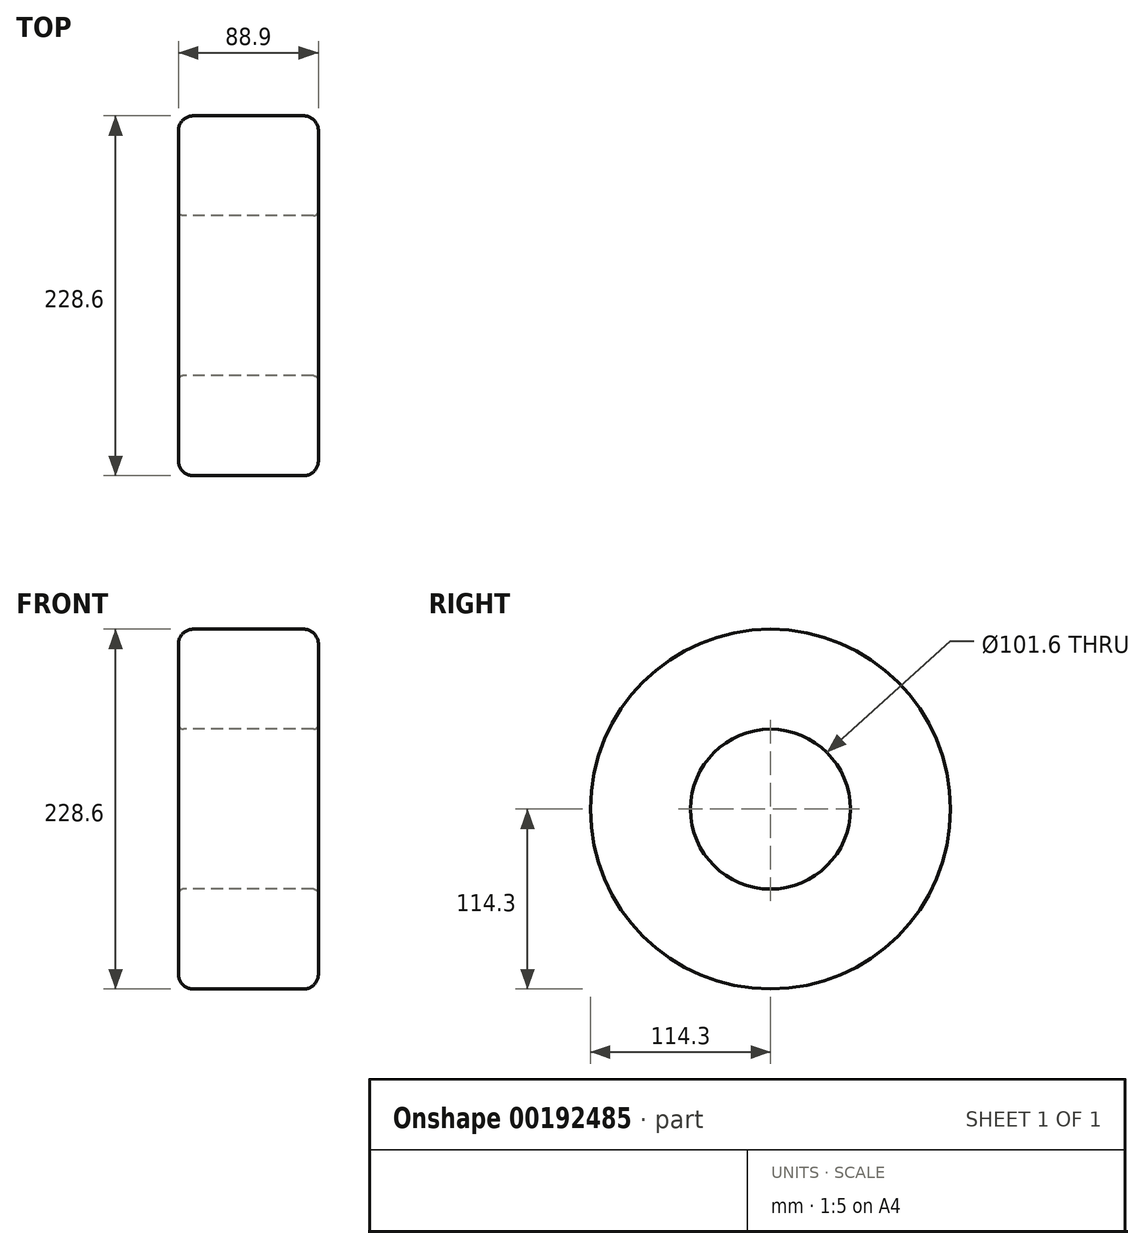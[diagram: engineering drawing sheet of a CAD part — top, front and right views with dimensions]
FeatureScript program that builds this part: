
annotation { "Feature Type Name" : "Feature", "Feature Type Description" : "" }
export const myFeature = defineFeature(function(context is Context, id is Id, definition is map)
    precondition{}
    {
        {
            var Q0;
            Q0=qCreatedBy(makeId("Front.planeOp"),FACE);
            var sketch = newSketch(context, id + "F0", { "sketchPlane" : qUnion([Q0])});
            skLineSegment(sketch, "E0.bottom", {"start": v(41.27, 50.8) * mm, "end": v(-41.27, 50.8) * mm});
            skLineSegment(sketch, "E0.top", {"start": v(34.93, 114.3) * mm, "end": v(-34.93, 114.3) * mm});
            skLineSegment(sketch, "E0.left", {"start": v(44.45, 53.98) * mm, "end": v(44.45, 104.78) * mm});
            skLineSegment(sketch, "E0.right", {"start": v(-44.45, 53.98) * mm, "end": v(-44.45, 104.78) * mm});
            skPoint(sketch, "E0.middle", {"position": v(0, 82.55) * mm});
            skPoint(sketch, "E1.visualSharp", {"position": v(-44.45, 114.3) * mm});
            skArc(sketch, "E1.filletArc", {"start": v(-34.93, 114.3) * mm, "mid": v(-41.66, 111.51) * mm, "end": v(-44.45, 104.78) * mm});
            skPoint(sketch, "E2.visualSharp", {"position": v(44.45, 114.3) * mm});
            skArc(sketch, "E2.filletArc", {"start": v(44.45, 104.78) * mm, "mid": v(41.66, 111.51) * mm, "end": v(34.93, 114.3) * mm});
            skPoint(sketch, "E3.visualSharp", {"position": v(-44.45, 50.8) * mm});
            skArc(sketch, "E3.filletArc", {"start": v(-44.45, 53.98) * mm, "mid": v(-43.52, 51.73) * mm, "end": v(-41.27, 50.8) * mm});
            skPoint(sketch, "E4.visualSharp", {"position": v(44.45, 50.8) * mm});
            skArc(sketch, "E4.filletArc", {"start": v(41.27, 50.8) * mm, "mid": v(43.52, 51.73) * mm, "end": v(44.45, 53.98) * mm});
            skLineSegment(sketch, "E5", {"start": v(-51.43, 0) * mm, "end": v(55.05, 0) * mm, "construction": true});
            skSolve(sketch);
        }
        {
            var Q0;
            Q0 = qSketchRegion(id + "F0", true);
            var Q1;
            Q1=sQuery(id+"F0.wireOp",EDGE,"E5");
            revolve(context, id + "F1", {"entities" : qUnion([Q0]), "axis" : qUnion([Q1]), "revolveType" : RevolveType.FULL});
        }
    });
